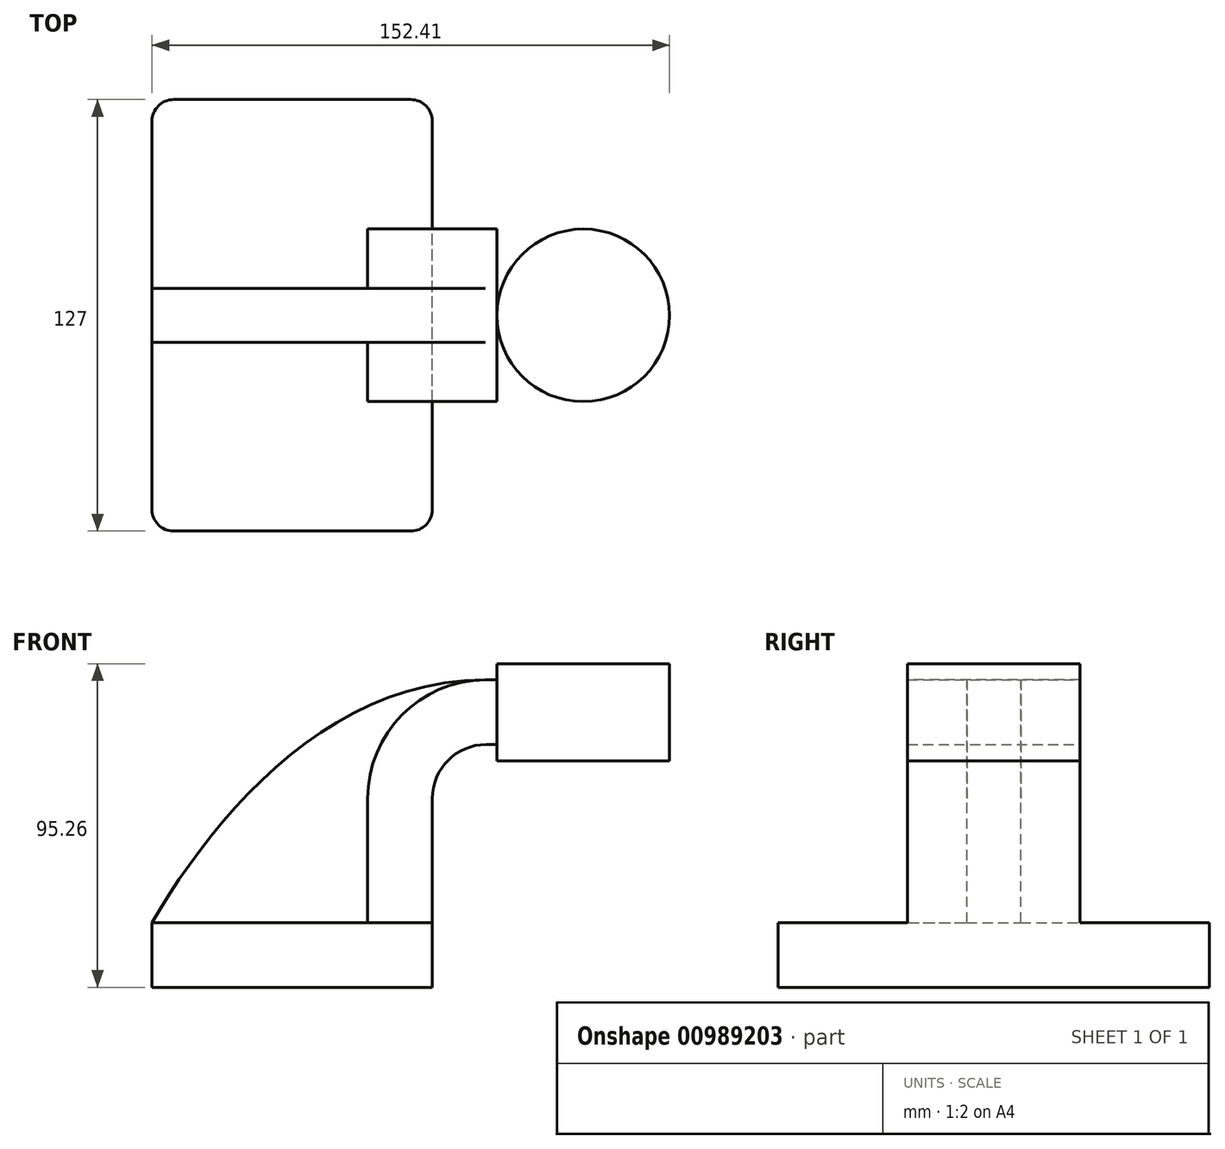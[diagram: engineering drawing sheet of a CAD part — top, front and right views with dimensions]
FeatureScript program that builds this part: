
annotation { "Feature Type Name" : "Feature", "Feature Type Description" : "" }
export const myFeature = defineFeature(function(context is Context, id is Id, definition is map)
    precondition{}
    {
        {
            var Q0;
            Q0=qCreatedBy(makeId("Front.planeOp"),FACE);
            var sketch = newSketch(context, id + "F0", { "sketchPlane" : qUnion([Q0])});
            skLineSegment(sketch, "E0.bottom", {"start": v(-41.28, -9.53) * mm, "end": v(41.28, -9.53) * mm});
            skLineSegment(sketch, "E0.top", {"start": v(-41.28, 9.53) * mm, "end": v(41.28, 9.53) * mm});
            skLineSegment(sketch, "E0.left", {"start": v(-41.28, -9.53) * mm, "end": v(-41.28, 9.53) * mm});
            skLineSegment(sketch, "E0.right", {"start": v(41.28, -9.53) * mm, "end": v(41.28, 9.53) * mm});
            skPoint(sketch, "E0.middle", {"position": v(0, 0) * mm});
            skLineSegment(sketch, "E1.bottom", {"start": v(111.12, 57.15) * mm, "end": v(60.32, 57.15) * mm});
            skLineSegment(sketch, "E1.top", {"start": v(111.12, 85.73) * mm, "end": v(60.33, 85.72) * mm});
            skLineSegment(sketch, "E1.left", {"start": v(111.12, 57.15) * mm, "end": v(111.12, 85.73) * mm});
            skLineSegment(sketch, "E1.right", {"start": v(60.32, 57.15) * mm, "end": v(60.32, 85.72) * mm});
            skPoint(sketch, "E1.middle", {"position": v(85.72, 71.44) * mm});
            skLineSegment(sketch, "E2", {"start": v(41.27, 9.52) * mm, "end": v(41.27, 46.05) * mm});
            skArc(sketch, "E3", {"start": v(41.27, 46.05) * mm, "mid": v(45.92, 57.28) * mm, "end": v(57.15, 61.93) * mm});
            skLineSegment(sketch, "E4", {"start": v(57.15, 61.93) * mm, "end": v(85.72, 61.93) * mm});
            skLineSegment(sketch, "E5", {"start": v(85.72, 61.93) * mm, "end": v(71.44, 61.93) * mm});
            skLineSegment(sketch, "E6.0", {"start": v(22.22, 9.52) * mm, "end": v(22.22, 46.05) * mm});
            skArc(sketch, "E7.0", {"start": v(22.22, 46.05) * mm, "mid": v(32.45, 70.75) * mm, "end": v(57.15, 80.98) * mm});
            skLineSegment(sketch, "E8.0", {"start": v(57.15, 80.98) * mm, "end": v(85.72, 80.98) * mm});
            skLineSegment(sketch, "E9", {"start": v(85.72, 57.15) * mm, "end": v(85.72, 85.73) * mm});
            skFitSpline(sketch, "E10", {"points": [v(-41.28, 9.52) * mm, v(57.15, 80.98) * mm], "startDerivative": vector(56.2, 95.53) * mm, "endDerivative": vector(140.59, 0.4) * mm});
            skSolve(sketch);
        }
        {
            var Q0;
            Q0=makeQuery(id+"F0.imprint","IMPRINT",FACE,{"disambiguationData":[TD([[makeQuery(id+"F0.imprint","IMPRINT",EDGE,{"derivedFrom":sQuery(id+"F0.wireOp",EDGE,"E0.bottom")}),1.0]])]});
            extrude(context, id + "F1", {"entities" : qUnion([Q0]), "endBound" : BoundingType.SYMMETRIC, "depth" : 127 * mm, "offsetDistance" : 25.4 * mm});
        }
        {
            var Q0;
            {var subQ1=sQuery(id+"F0.wireOp",EDGE,"E2");Q0=makeQuery(id+"F0.imprint","IMPRINT",FACE,{"disambiguationData":[TD([[makeQuery(id+"F0.imprint","IMPRINT",EDGE,{"derivedFrom":subQ1}),1.0]])]});}
            var Q1;
            {var subQ0=sQuery(id+"F0.wireOp",EDGE,"E5");Q1=makeQuery(id+"F0.imprint","IMPRINT",FACE,{"disambiguationData":[TD([[makeQuery(id+"F0.imprint","IMPRINT",EDGE,{"derivedFrom":subQ0}),-1.0]])]});}
            extrude(context, id + "F2", {"entities" : qUnion([Q0, Q1]), "operationType" : NewBodyOperationType.ADD, "endBound" : BoundingType.SYMMETRIC, "depth" : 50.8 * mm, "offsetDistance" : 25.4 * mm});
        }
        {
            var Q0;
            {var subQ3=sQuery(id+"F0.wireOp",EDGE,"E6.0");Q0=makeQuery(id+"F0.imprint","IMPRINT",FACE,{"disambiguationData":[TD([[makeQuery(id+"F0.imprint","IMPRINT",EDGE,{"derivedFrom":subQ3}),1.0]])]});}
            extrude(context, id + "F3", {"entities" : qUnion([Q0]), "operationType" : NewBodyOperationType.ADD, "endBound" : BoundingType.SYMMETRIC, "depth" : 15.88 * mm, "offsetDistance" : 25.4 * mm});
        }
        {
            var Q0;
            {var subQ0=sQuery(id+"F0.wireOp",EDGE,"E1.left");Q0=makeQuery(id+"F0.imprint","IMPRINT",FACE,{"disambiguationData":[TD([[makeQuery(id+"F0.imprint","IMPRINT",EDGE,{"derivedFrom":subQ0}),1.0]])]});}
            var Q1;
            Q1=sQuery(id+"F0.wireOp",EDGE,"E9");
            revolve(context, id + "F4", {"operationType" : NewBodyOperationType.ADD, "surfaceOperationType" : NewSurfaceOperationType.NEW, "entities" : qUnion([Q0]), "axis" : qUnion([Q1]), "revolveType" : RevolveType.FULL});
        }
        {
            var Q0;
            Q0=makeQuery(id+"F1.opExtrude","CAP_EDGE",EDGE,{"disambiguationData":[OSD([sQuery(id+"F0.wireOp",EDGE,"E0.left")])],"isStart":false});
            var Q1;
            Q1=makeQuery(id+"F1.opExtrude","CAP_EDGE",EDGE,{"disambiguationData":[OSD([sQuery(id+"F0.wireOp",EDGE,"E0.right")])],"isStart":false});
            var Q2;
            Q2=makeQuery(id+"F1.opExtrude","CAP_EDGE",EDGE,{"disambiguationData":[OSD([sQuery(id+"F0.wireOp",EDGE,"E0.right")])],"isStart":true});
            var Q3;
            Q3=makeQuery(id+"F1.opExtrude","CAP_EDGE",EDGE,{"disambiguationData":[OSD([sQuery(id+"F0.wireOp",EDGE,"E0.left")])],"isStart":true});
            fillet(context, id + "F5", {"entities" : qUnion([Q0, Q1, Q2, Q3]), "radius" : 6.35 * mm, "tangentPropagation" : true, "allowEdgeOverflow" : false});
        }
    });
